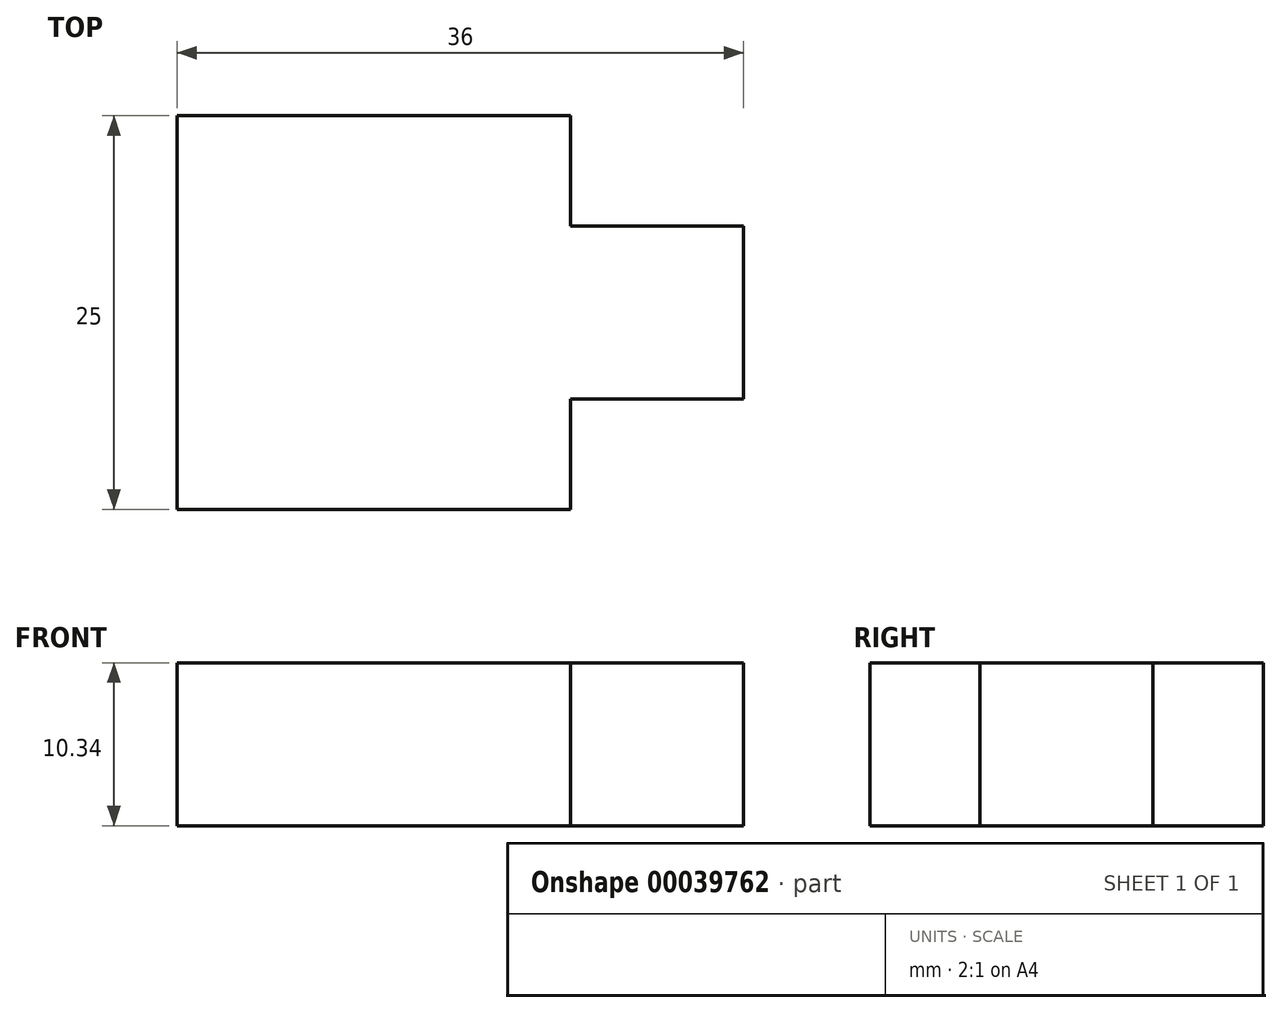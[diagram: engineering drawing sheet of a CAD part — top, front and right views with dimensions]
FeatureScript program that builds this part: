
annotation { "Feature Type Name" : "Feature", "Feature Type Description" : "" }
export const myFeature = defineFeature(function(context is Context, id is Id, definition is map)
    precondition{}
    {
        {
            var Q0;
            Q0=qCreatedBy(makeId("Top.planeOp"),FACE);
            var sketch = newSketch(context, id + "F0", { "sketchPlane" : qUnion([Q0])});
            skLineSegment(sketch, "E0.bottom", {"start": v(-36, 46.91) * mm, "end": v(-11, 46.91) * mm});
            skLineSegment(sketch, "E0.top", {"start": v(-36, 21.91) * mm, "end": v(-11, 21.91) * mm});
            skLineSegment(sketch, "E0.left", {"start": v(-36, 46.91) * mm, "end": v(-36, 21.91) * mm});
            skLineSegment(sketch, "E0.right", {"start": v(-11, 46.91) * mm, "end": v(-11, 21.91) * mm});
            skLineSegment(sketch, "E1.bottom", {"start": v(-11, 39.91) * mm, "end": v(0, 39.91) * mm});
            skLineSegment(sketch, "E1.top", {"start": v(-11, 28.91) * mm, "end": v(0, 28.91) * mm});
            skLineSegment(sketch, "E1.left", {"start": v(-11, 39.91) * mm, "end": v(-11, 28.91) * mm});
            skLineSegment(sketch, "E1.right", {"start": v(0, 39.91) * mm, "end": v(0, 28.91) * mm});
            skLineSegment(sketch, "E2.bottom", {"start": v(-29, 21.91) * mm, "end": v(-18, 21.91) * mm});
            skLineSegment(sketch, "E2.top", {"start": v(-29, 10.91) * mm, "end": v(-18, 10.91) * mm});
            skLineSegment(sketch, "E2.left", {"start": v(-29, 21.91) * mm, "end": v(-29, 10.91) * mm});
            skLineSegment(sketch, "E2.right", {"start": v(-18, 21.91) * mm, "end": v(-18, 10.91) * mm});
            skSolve(sketch);
        }
        {
            var Q0;
            Q0=makeQuery(id+"F0.imprint","IMPRINT",FACE,{"disambiguationData":[TD([[makeQuery(id+"F0.imprint","IMPRINT",EDGE,{"derivedFrom":sQuery(id+"F0.wireOp",EDGE,"E2.bottom")}),-1.0]])]});
            var Q1;
            Q1=makeQuery(id+"F0.imprint","IMPRINT",FACE,{"disambiguationData":[TD([[makeQuery(id+"F0.imprint","IMPRINT",EDGE,{"derivedFrom":sQuery(id+"F0.wireOp",EDGE,"E1.bottom")}),-1.0]])]});
            var Q2;
            {var subQ4=sQuery(id+"F0.wireOp",EDGE,"E0.bottom");Q2=makeQuery(id+"F0.imprint","IMPRINT",FACE,{"disambiguationData":[TD([[makeQuery(id+"F0.imprint","IMPRINT",EDGE,{"derivedFrom":subQ4}),-1.0]])]});}
            extrude(context, id + "F1", {"entities" : qUnion([Q0, Q1, Q2]), "depth" : 10.34 * mm});
        }
    });
